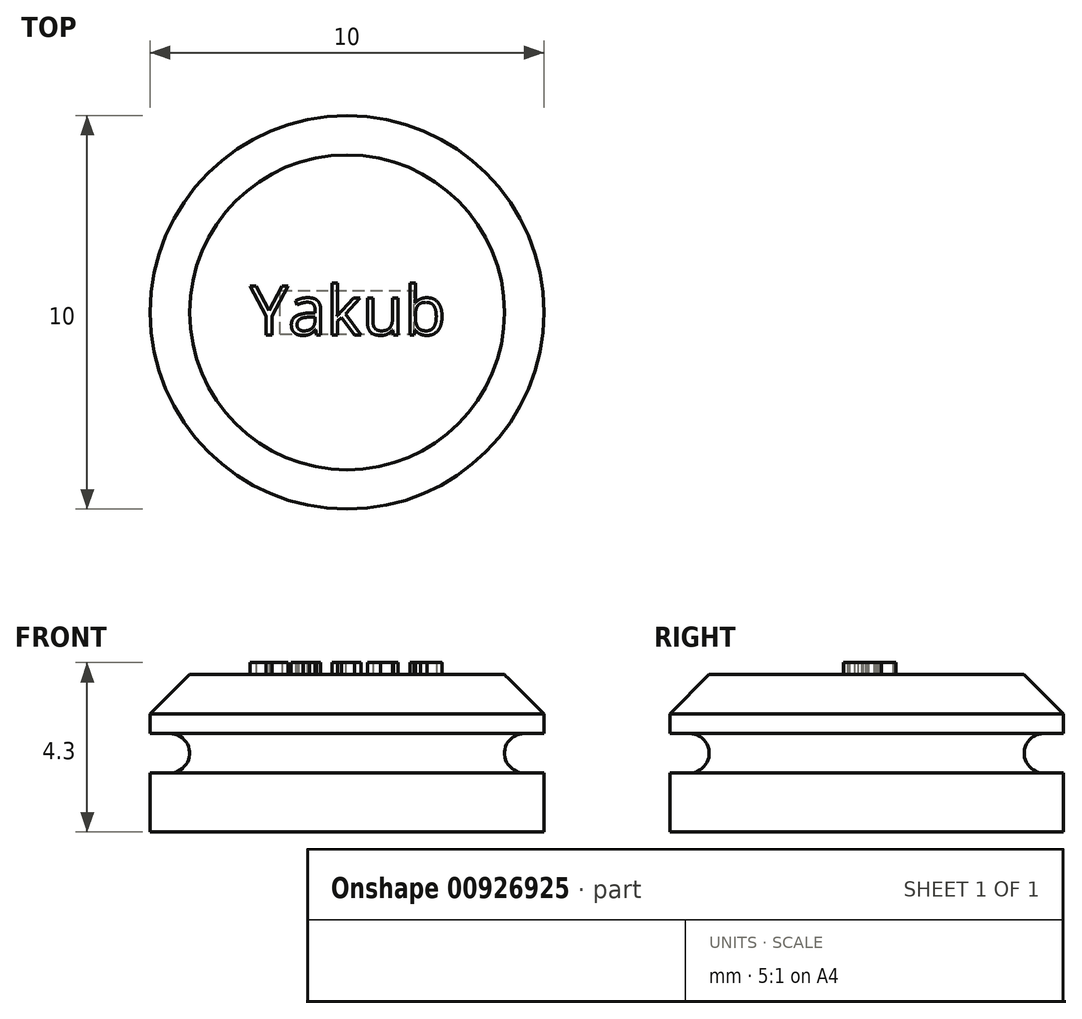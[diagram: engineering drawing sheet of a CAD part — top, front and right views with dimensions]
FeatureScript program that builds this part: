
annotation { "Feature Type Name" : "Feature", "Feature Type Description" : "" }
export const myFeature = defineFeature(function(context is Context, id is Id, definition is map)
    precondition{}
    {
        {
            var Q0;
            Q0=qCreatedBy(makeId("Front.planeOp"),FACE);
            var sketch = newSketch(context, id + "F0", { "sketchPlane" : qUnion([Q0])});
            skLineSegment(sketch, "E0", {"start": v(0, 4) * mm, "end": v(0, 0) * mm});
            skLineSegment(sketch, "E1", {"start": v(0, 0) * mm, "end": v(5, 0) * mm});
            skLineSegment(sketch, "E2", {"start": v(0, 4) * mm, "end": v(5, 4) * mm});
            skLineSegment(sketch, "E3", {"start": v(5, 4) * mm, "end": v(5, 0) * mm});
            skLineSegment(sketch, "E4", {"start": v(5, 2.5) * mm, "end": v(4, 2.5) * mm});
            skLineSegment(sketch, "E5", {"start": v(4, 2.5) * mm, "end": v(4, 1.5) * mm});
            skLineSegment(sketch, "E6", {"start": v(4, 1.5) * mm, "end": v(5, 1.5) * mm});
            skSolve(sketch);
        }
        {
            var Q0;
            Q0=makeQuery(id+"F0.imprint","IMPRINT",FACE,{"disambiguationData":[TD([[makeQuery(id+"F0.imprint","IMPRINT",EDGE,{"derivedFrom":sQuery(id+"F0.wireOp",EDGE,"E0")}),1.0]])]});
            var Q1;
            Q1=sQuery(id+"F0.wireOp",EDGE,"E0");
            revolve(context, id + "F1", {"surfaceOperationType" : NewSurfaceOperationType.NEW, "entities" : qUnion([Q0]), "axis" : qUnion([Q1]), "revolveType" : RevolveType.FULL});
        }
        {
            var Q0;
            Q0=makeQuery(id+"F1.opRevolve","SWEPT_EDGE",EDGE,{"disambiguationData":[OSD([sQuery(id+"F0.wireOp",EDGE,"E2"),sQuery(id+"F0.wireOp",EDGE,"E3")])]});
            chamfer(context, id + "F2", {"entities" : qUnion([Q0]), "width" : 1 * mm, "tangentPropagation" : true});
        }
        {
            var Q0;
            Q0=makeQuery(id+"F1.opRevolve","SWEPT_FACE",FACE,{"disambiguationData":[OSD([sQuery(id+"F0.wireOp",EDGE,"E1")])]});
            var sketch = newSketch(context, id + "F3", { "sketchPlane" : qUnion([Q0])});
            skLineSegment(sketch, "E7.bottom", {"start": v(-1.7, 0.55) * mm, "end": v(1.7, 0.55) * mm});
            skLineSegment(sketch, "E7.top", {"start": v(-1.7, -0.55) * mm, "end": v(1.7, -0.55) * mm});
            skLineSegment(sketch, "E7.left", {"start": v(-1.7, 0.55) * mm, "end": v(-1.7, -0.55) * mm});
            skLineSegment(sketch, "E7.right", {"start": v(1.7, 0.55) * mm, "end": v(1.7, -0.55) * mm});
            skPoint(sketch, "E7.middle", {"position": v(0, 0) * mm});
            skSolve(sketch);
        }
        {
            var Q0;
            Q0=makeQuery(id+"F3.imprint","IMPRINT",FACE,{"disambiguationData":[TD([[makeQuery(id+"F3.imprint","IMPRINT",EDGE,{"derivedFrom":sQuery(id+"F3.wireOp",EDGE,"E7.bottom")}),-1.0]])]});
            extrude(context, id + "F4", {"entities" : qUnion([Q0]), "operationType" : NewBodyOperationType.REMOVE, "oppositeDirection" : true, "depth" : 3 * mm, "offsetDistance" : 25 * mm});
        }
        {
            var Q0;
            Q0=makeQuery(id+"F1.opRevolve","SWEPT_EDGE",EDGE,{"disambiguationData":[OSD([sQuery(id+"F0.wireOp",EDGE,"E5"),sQuery(id+"F0.wireOp",EDGE,"E6")])]});
            var Q1;
            Q1=makeQuery(id+"F1.opRevolve","SWEPT_EDGE",EDGE,{"disambiguationData":[OSD([sQuery(id+"F0.wireOp",EDGE,"E4"),sQuery(id+"F0.wireOp",EDGE,"E5")])]});
            fillet(context, id + "F5", {"entities" : qUnion([Q0, Q1]), "radius" : 0.5 * mm, "tangentPropagation" : true, "allowEdgeOverflow" : false});
        }
        {
            var Q0;
            Q0=makeQuery(id+"F1.opRevolve","SWEPT_FACE",FACE,{"disambiguationData":[OSD([sQuery(id+"F0.wireOp",EDGE,"E2")])]});
            var sketch = newSketch(context, id + "F6", { "sketchPlane" : qUnion([Q0])});
            skText(sketch, "E8", { "text": "Yakub", "fontName": "OpenSans-Regular.ttf"});
            const initialGuessF6  = {"E8": [-0.00247, -0.00057, 1, 0, 0.00125]};
            skSetInitialGuess(sketch, initialGuessF6);
            skSolve(sketch);
        }
        {
            var Q0;
            Q0 = qSketchRegion(id + "F6", true);
            extrude(context, id + "F7", {"entities" : qUnion([Q0]), "operationType" : NewBodyOperationType.ADD, "depth" : 0.3 * mm, "offsetDistance" : 25 * mm});
        }
    });
